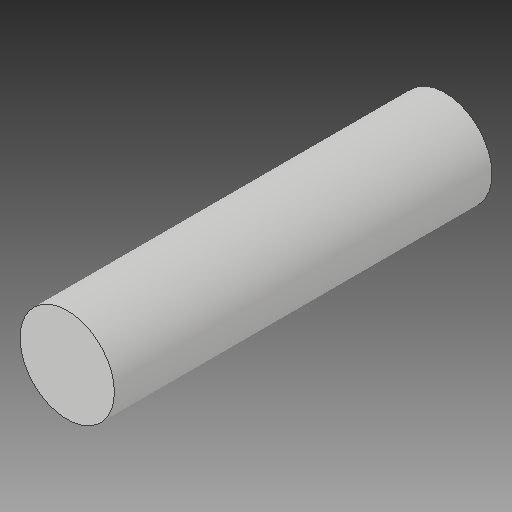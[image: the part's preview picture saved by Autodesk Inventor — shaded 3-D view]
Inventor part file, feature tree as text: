
AUTODESK INVENTOR PART (.ipt)
format: ipt  version: 2017 (Build 210142000, 142)  size: 86,528 bytes
history: native  units: in
note: dims shown in document units (in); Inventor stores cm internally (conversion verified against a paired STEP export)
features: extrude x1, sketch x1
ambient origin geometry x8: Origin, YZ Plane, XZ Plane, XY Plane, X Axis, Y Axis, Z Axis, Center Point
bodies: Solid1 (feature_tree)
feature tree (2):
  extrude  "Extrusion1"  Depth=3.0in TaperAngle=0.0deg
  sketch  "Sketch1"  dims[d0=0.75in d1=3.0in d2=0.0in]
